# Revit family: Vent_Cap-Navien-Outdoor-Kit
name_source: partatom
category: Mechanical Equipment
revit_build: Autodesk Revit 2018 (Build: 20190510_1515(x64)
units: mm (PartAtom-declared; Revit-internal decimal feet)

## family parameters
Cut with Voids When Loaded = No
Host = Face
OmniClass Number = 23.65.35.11
OmniClass Title = Supply Water Heaters
Part Type = Normal
Room Calculation Point = No
Round Connector Dimension = Use Diameter
Shared = No

## types (1)
- Outdoor Vent Cap Kit (NPN-U Only)
    Assembly Code = D3010500
    Default Elevation = 48 "
    Depth = 9.94 "
    Description = Designed for NPN-U when installing unit outdoors. Required for NPN-U outdoor installations.
    Finish = Polypropylene - Navien - White
    Height = 4.72 "
    Installation Type = Outdoor Vent Cover
    Keynote = 22 33 00.A1
    Manufacturer = Navien, Inc.
    Manufacturer Fax Number = (949) 420-0430
    Model = 30023991A
    Product Documentation Link = https://www.navieninc.com
    Product Name = Outdoor Vent Cap Kit (NPN-U Only)
    Product Page URL = https://www.navieninc.com
    URL = https://www.navieninc.com
    Version = 2018 - v1.0.a
    Warranty = https://www.navieninc.com
    Weight = 0.00 lbf
    Width = 14.46 "

## geometry (parser evidence)
native form markers: Sweep x2
no freeform markers — native parametric forms only
